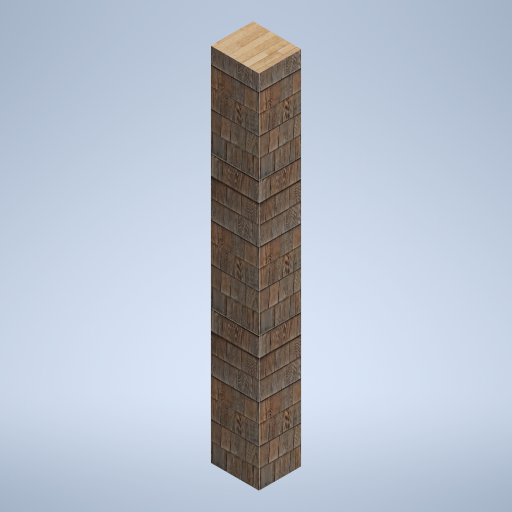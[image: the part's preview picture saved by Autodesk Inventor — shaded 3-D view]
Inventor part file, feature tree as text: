
AUTODESK INVENTOR PART (.ipt)
format: ipt  version: 2024.2 (Build 282272000, 272)  size: 356,352 bytes
history: native  units: in
note: dims shown in document units (in); Inventor stores cm internally (conversion verified against a paired STEP export)
features: other x3, sketch x1
ambient origin geometry x8: Origin, YZ Plane, XZ Plane, XY Plane, X Axis, Y Axis, Z Axis, Center Point
bodies: Solid1 (feature_tree)
feature tree (4):
  other  "support_column_02_MIR.ipt"
  other  "Solid1::support_column_02_MIR.ipt"
  other  "TaggingFeature1"
  sketch  "Sketch1"  dims[d0=0.3937in]
